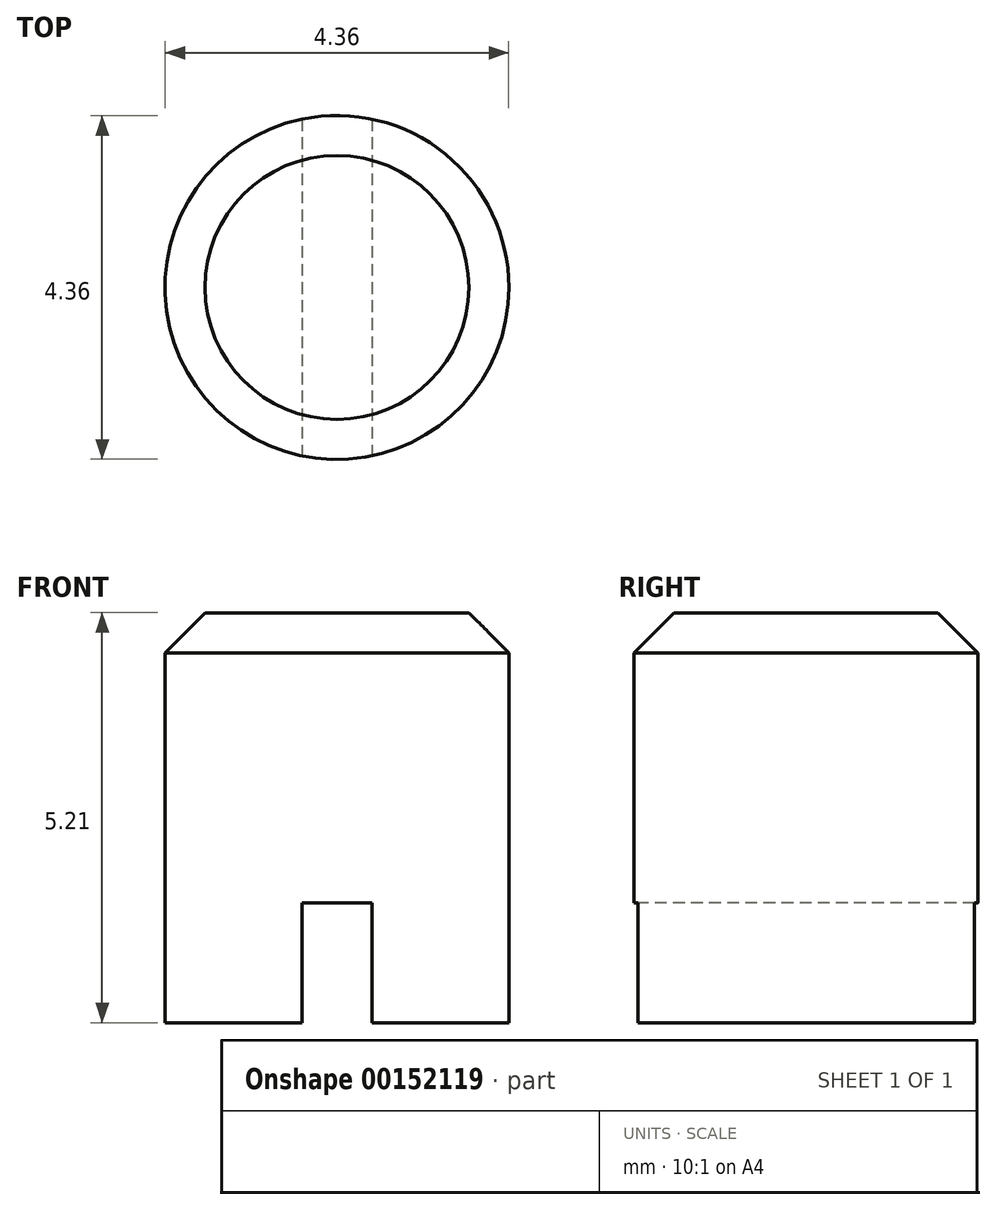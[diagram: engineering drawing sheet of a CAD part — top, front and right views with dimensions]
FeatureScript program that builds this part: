
annotation { "Feature Type Name" : "Feature", "Feature Type Description" : "" }
export const myFeature = defineFeature(function(context is Context, id is Id, definition is map)
    precondition{}
    {
        {
            var Q0;
            Q0=qCreatedBy(makeId("Top.planeOp"),FACE);
            var sketch = newSketch(context, id + "F0", { "sketchPlane" : qUnion([Q0])});
            skCircle(sketch, "E0", {"center": v(0, 0) * mm, "radius": 2.18 * mm});
            skSolve(sketch);
        }
        {
            var Q0;
            Q0=makeQuery(id+"F0.imprint","IMPRINT",FACE,{"disambiguationData":[TD([[makeQuery(id+"F0.imprint","IMPRINT",EDGE,{"derivedFrom":sQuery(id+"F0.wireOp",EDGE,"E0")}),1.0]])]});
            extrude(context, id + "F1", {"entities" : qUnion([Q0]), "depth" : 5.2 * mm});
        }
        {
            var Q0;
            Q0=qCreatedBy(makeId("Front.planeOp"),FACE);
            var sketch = newSketch(context, id + "F2", { "sketchPlane" : qUnion([Q0])});
            skLineSegment(sketch, "E1.bottom", {"start": v(0.44, 1.52) * mm, "end": v(-0.44, 1.52) * mm});
            skLineSegment(sketch, "E1.top", {"start": v(0.44, -1.52) * mm, "end": v(-0.44, -1.52) * mm});
            skLineSegment(sketch, "E1.left", {"start": v(0.44, 1.52) * mm, "end": v(0.44, -1.52) * mm});
            skLineSegment(sketch, "E1.right", {"start": v(-0.44, 1.52) * mm, "end": v(-0.44, -1.52) * mm});
            skPoint(sketch, "E1.middle", {"position": v(0, 0) * mm});
            skSolve(sketch);
        }
        {
            var Q0;
            Q0=makeQuery(id+"F2.imprint","IMPRINT",FACE,{"disambiguationData":[TD([[makeQuery(id+"F2.imprint","IMPRINT",EDGE,{"derivedFrom":sQuery(id+"F2.wireOp",EDGE,"E1.bottom")}),1.0]])]});
            extrude(context, id + "F3", {"entities" : qUnion([Q0]), "operationType" : NewBodyOperationType.REMOVE, "endBound" : BoundingType.SYMMETRIC, "oppositeDirection" : true, "depth" : 25.4 * mm});
        }
        {
            var Q0;
            Q0=makeQuery(id+"F1.opExtrude","CAP_EDGE",EDGE,{"disambiguationData":[OSD([sQuery(id+"F0.wireOp",EDGE,"E0")])],"isStart":false});
            chamfer(context, id + "F4", {"entities" : qUnion([Q0]), "width" : 0.5 * mm, "tangentPropagation" : true});
        }
    });
